# Revit family: Waste_Receptacle-Bobrick-TrimLineSeries-B-35639
name_source: partatom
category: Specialty Equipment
revit_build: Autodesk Revit 2014 (Build: 20130308_1515(x64)
units: mm (PartAtom-declared; Revit-internal decimal feet)

## types (1)
- B-35639
    ADA Compliant = Yes
    Assembly Code = E1090900
    Default Elevation = 47"
    Description = TrimLineSeries™ Surface-Mounted Waste Receptacle
    Height = 28 3/16"
    Installation Type = Surface-Mounted
    Length = 4 1/2"
    Manufacturer = Bobrick Washroom Equipment, Inc.
    Material = Stainless Steel-Bobrick-Type 304-Satin
    Model = B-35639
    Price = Prices may vary. Please consult Manufacturer Representative for most up-to-date price list.
    Product Page URL = http://www.bobrick.com
    Specification = Surface-mounted paper waste receptacle shall be Type-304 stainless steel with all-welded construction; exposed surfaces shall have satin finish. Door shall be Type-304, 18 gauge (1.2mm) secured to cabinet with a concealed, full-length stainless steel piano-hinge, cable door-swing limiter and equipped with a tumbler lock keyed like other Bobrick washroom accessories. Waste receptacle shall be Type-304, heavy-gauge stainless steel. All-welded construction with a capacity of 3-gal. (11.3-L).
    URL = http://www.bobrick.com
    Warranty Information = 1 Year Limited Warranty
    Width = 14 3/16"

## geometry (parser evidence)
native form markers: Sweep x3
no freeform markers — native parametric forms only
